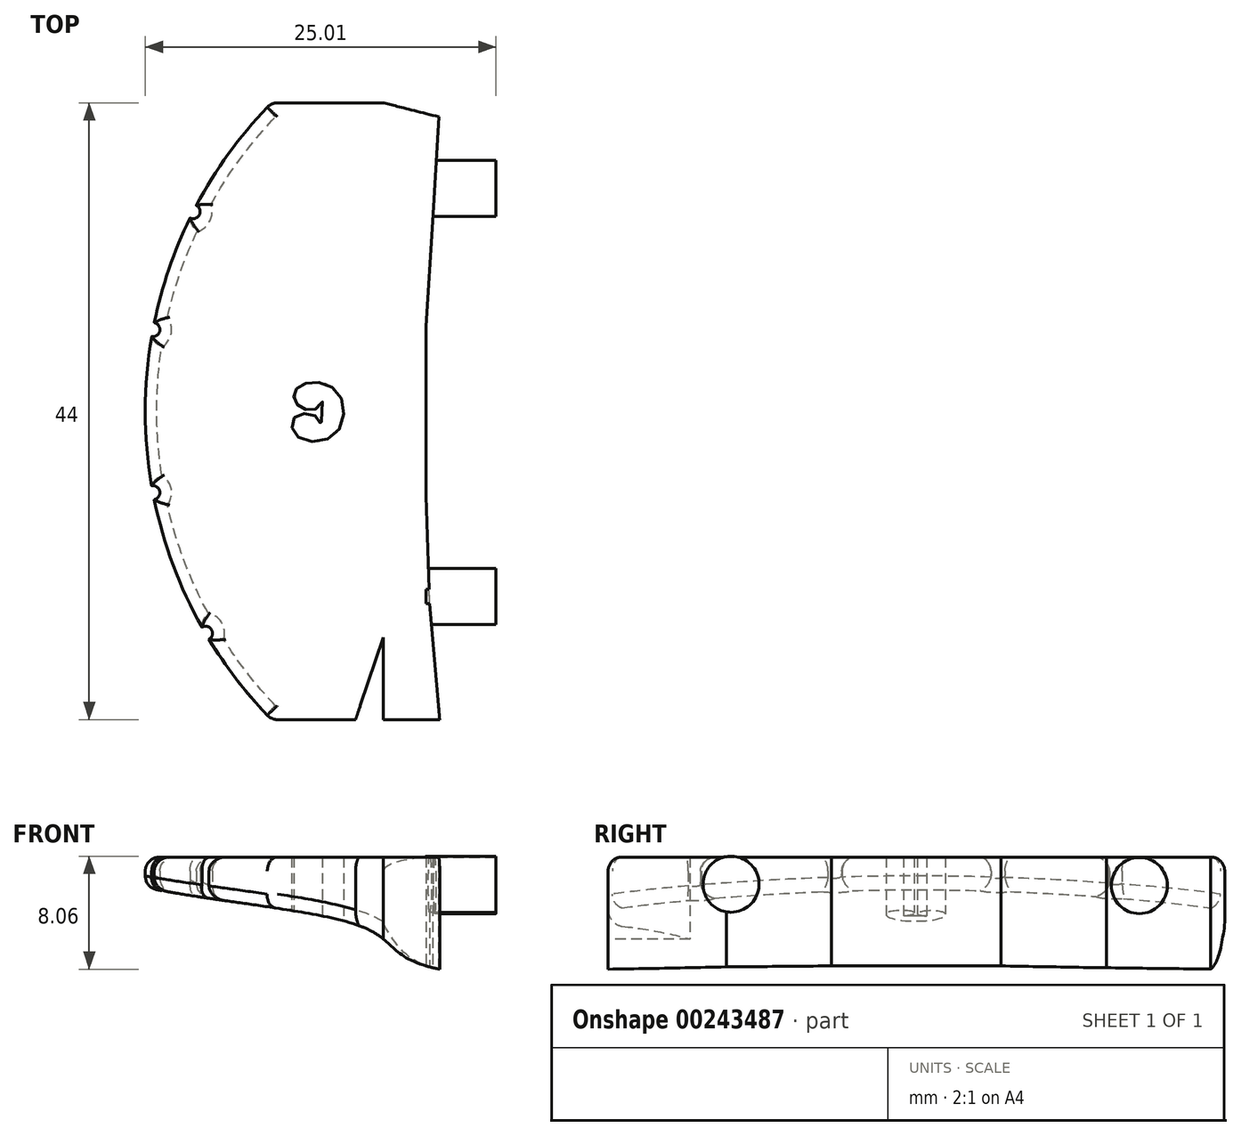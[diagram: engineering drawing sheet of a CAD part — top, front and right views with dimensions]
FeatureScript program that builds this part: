
annotation { "Feature Type Name" : "Feature", "Feature Type Description" : "" }
export const myFeature = defineFeature(function(context is Context, id is Id, definition is map)
    precondition{}
    {
        {
            var Q0;
            Q0=qCreatedBy(makeId("Top.planeOp"),FACE);
            var sketch = newSketch(context, id + "F0", { "sketchPlane" : qUnion([Q0])});
            skLineSegment(sketch, "E0.bottom", {"start": v(0, 0) * mm, "end": v(12, 0) * mm});
            skLineSegment(sketch, "E0.top", {"start": v(0, 44) * mm, "end": v(12, 44) * mm});
            skLineSegment(sketch, "E0.left", {"start": v(0, 0) * mm, "end": v(0, 44) * mm});
            skLineSegment(sketch, "E0.right", {"start": v(12, 0) * mm, "end": v(12, 44) * mm});
            skPoint(sketch, "E1", {"position": v(0, 22) * mm});
            skArc(sketch, "E2", {"start": v(0, 44) * mm, "mid": v(-9, 22) * mm, "end": v(0, 0) * mm});
            skLineSegment(sketch, "E3", {"start": v(0, 0) * mm, "end": v(0, 3.52) * mm, "construction": true});
            skLineSegment(sketch, "E4", {"start": v(0, 40.48) * mm, "end": v(0, 44) * mm, "construction": true});
            skLineSegment(sketch, "E5", {"start": v(18.87, 22) * mm, "end": v(22.39, 22) * mm, "construction": true});
            skPoint(sketch, "E6", {"position": v(-9, 22) * mm});
            skCircle(sketch, "E7", {"center": v(-5.59, 36.24) * mm, "radius": 0.5 * mm});
            skCircle(sketch, "E8", {"center": v(-8.45, 27.82) * mm, "radius": 0.5 * mm});
            skCircle(sketch, "E9", {"center": v(-8.46, 16.2) * mm, "radius": 0.5 * mm});
            skCircle(sketch, "E10", {"center": v(-4.71, 6.16) * mm, "radius": 0.5 * mm});
            skPoint(sketch, "E11", {"position": v(0, 40.69) * mm});
            skLineSegment(sketch, "E12", {"start": v(12, 44) * mm, "end": v(11.52, 35.55) * mm});
            skLineSegment(sketch, "E13", {"start": v(11.52, 35.55) * mm, "end": v(11.01, 28.04) * mm});
            skLineSegment(sketch, "E14", {"start": v(11.01, 28.04) * mm, "end": v(11.01, 15.95) * mm});
            skLineSegment(sketch, "E15", {"start": v(11.01, 15.95) * mm, "end": v(11.28, 8.43) * mm});
            skLineSegment(sketch, "E16", {"start": v(11.28, 8.43) * mm, "end": v(12, 0) * mm});
            skLineSegment(sketch, "E17", {"start": v(7.97, 0) * mm, "end": v(7.97, 5.86) * mm});
            skLineSegment(sketch, "E18", {"start": v(7.97, 5.86) * mm, "end": v(6, 0) * mm});
            skFitSpline(sketch, "E19", {"points": [v(3.6, 22) * mm, v(3.63, 22.75) * mm, v(3.3, 22.24) * mm, v(2.12, 22.24) * mm, v(1.6, 23.16) * mm, v(2.47, 24) * mm, v(4.75, 23.31) * mm, v(4.57, 20.39) * mm, v(1.82, 20.21) * mm, v(1.66, 21.56) * mm, v(3.15, 21.65) * mm, v(3.54, 21.08) * mm, v(3.6, 22) * mm]});
            skSolve(sketch);
        }
        {
            var Q0;
            Q0=makeQuery(id+"F0.imprint","IMPRINT",FACE,{"disambiguationData":[TD([[makeQuery(id+"F0.imprint","IMPRINT",EDGE,{"derivedFrom":sQuery(id+"F0.wireOp",EDGE,"E0.bottom")}),1.0]])]});
            var Q1;
            {var subQ8=sQuery(id+"F0.wireOp",EDGE,"E0.left");Q1=makeQuery(id+"F0.imprint","IMPRINT",FACE,{"disambiguationData":[TD([[makeQuery(id+"F0.imprint","IMPRINT",EDGE,{"derivedFrom":subQ8}),1.0]])]});}
            extrude(context, id + "F1", {"entities" : qUnion([Q0, Q1]), "depth" : 8 * mm, "offsetDistance" : 25 * mm});
        }
        {
            var Q0;
            Q0=makeQuery(id+"F1.opExtrude","SWEPT_FACE",FACE,{"disambiguationData":[OSD([sQuery(id+"F0.wireOp",EDGE,"E0.bottom")])]});
            var sketch = newSketch(context, id + "F2", { "sketchPlane" : qUnion([Q0])});
            skLineSegment(sketch, "E20.bottom", {"start": v(12, 0) * mm, "end": v(-10.64, 0) * mm});
            skLineSegment(sketch, "E20.left", {"start": v(12, 0) * mm, "end": v(12, 2.4) * mm});
            skLineSegment(sketch, "E21", {"start": v(12, 8) * mm, "end": v(12, 2.4) * mm});
            skLineSegment(sketch, "E22", {"start": v(-10.64, 6.2) * mm, "end": v(-10.64, 0) * mm});
            skPoint(sketch, "E23.1.internal.snap0", {"position": v(0, 4) * mm});
            skFitSpline(sketch, "E23", {"points": [v(-10.64, 6.2) * mm, v(7.08, 2.75) * mm, v(12, 0) * mm], "startDerivative": vector(27.55, -6.78) * mm, "endDerivative": vector(27.26, -5.3) * mm});
            skSolve(sketch);
        }
        {
            var Q0;
            Q0 = qSketchRegion(id + "F2", true);
            extrude(context, id + "F3", {"entities" : qUnion([Q0]), "operationType" : NewBodyOperationType.REMOVE, "oppositeDirection" : true, "depth" : 50 * mm, "offsetDistance" : 25 * mm});
        }
        {
            var Q0;
            Q0=makeQuery(id+"F1.opExtrude","CAP_EDGE",EDGE,{"disambiguationData":[OSD([sQuery(id+"F0.wireOp",EDGE,"E2")])],"isStart":false});
            var Q1;
            Q1=makeQuery(id+"F1.opExtrude","CAP_EDGE",EDGE,{"disambiguationData":[OSD([sQuery(id+"F0.wireOp",EDGE,"E7")])],"isStart":false});
            var Q2;
            Q2=makeQuery(id+"F3.boolean.opBoolean","INTERSECT",EDGE,{"derivedFrom":[makeQuery(id+"F1.opExtrude","SWEPT_FACE",FACE,{"disambiguationData":[OSD([sQuery(id+"F0.wireOp",EDGE,"E8")])]}),makeQuery(id+"F3.opExtrude","SWEPT_FACE",FACE,{"disambiguationData":[OSD([sQuery(id+"F2.wireOp",EDGE,"E23")])]})]});
            var Q3;
            Q3=makeQuery(id+"F1.opExtrude","CAP_EDGE",EDGE,{"disambiguationData":[OSD([sQuery(id+"F0.wireOp",EDGE,"E8")])],"isStart":false});
            var Q4;
            Q4=makeQuery(id+"F3.boolean.opBoolean","INTERSECT",EDGE,{"derivedFrom":[makeQuery(id+"F1.opExtrude","SWEPT_FACE",FACE,{"disambiguationData":[OSD([sQuery(id+"F0.wireOp",EDGE,"E9")])]}),makeQuery(id+"F3.opExtrude","SWEPT_FACE",FACE,{"disambiguationData":[OSD([sQuery(id+"F2.wireOp",EDGE,"E23")])]})]});
            var Q5;
            Q5=makeQuery(id+"F3.boolean.opBoolean","INTERSECT",EDGE,{"derivedFrom":[makeQuery(id+"F1.opExtrude","SWEPT_FACE",FACE,{"disambiguationData":[OSD([sQuery(id+"F0.wireOp",EDGE,"E10")])]}),makeQuery(id+"F3.opExtrude","SWEPT_FACE",FACE,{"disambiguationData":[OSD([sQuery(id+"F2.wireOp",EDGE,"E23")])]})]});
            var Q6;
            Q6=makeQuery(id+"F1.opExtrude","CAP_EDGE",EDGE,{"disambiguationData":[OSD([sQuery(id+"F0.wireOp",EDGE,"E9")])],"isStart":false});
            var Q7;
            Q7=makeQuery(id+"F1.opExtrude","CAP_EDGE",EDGE,{"disambiguationData":[OSD([sQuery(id+"F0.wireOp",EDGE,"E10")])],"isStart":false});
            var Q8;
            {var subQ0=sQuery(id+"F0.wireOp",EDGE,"E2");Q8=makeQuery(id+"F3.boolean.opBoolean","INTERSECT",EDGE,{"derivedFrom":[makeQuery(id+"F1.opExtrude","SWEPT_FACE",FACE,{"disambiguationData":[OSD([subQ0]),TDD([makeQuery(id+"F0.imprint","IMPRINT",EDGE,{"disambiguationData":[TD([[makeQuery(id+"F0.imprint","INTERSECT",VERTEX,{"disambiguationData":[OD(1.0)],"derivedFrom":[subQ0,sQuery(id+"F0.wireOp",EDGE,"E7")]}),-1.0]])],"derivedFrom":subQ0})])]}),makeQuery(id+"F3.opExtrude","SWEPT_FACE",FACE,{"disambiguationData":[OSD([sQuery(id+"F2.wireOp",EDGE,"E23")])]})]});}
            var Q9;
            {var subQ0=sQuery(id+"F0.wireOp",EDGE,"E2");Q9=makeQuery(id+"F3.boolean.opBoolean","INTERSECT",EDGE,{"derivedFrom":[makeQuery(id+"F1.opExtrude","SWEPT_FACE",FACE,{"disambiguationData":[OSD([subQ0]),TDD([makeQuery(id+"F0.imprint","IMPRINT",EDGE,{"disambiguationData":[TD([[makeQuery(id+"F0.imprint","INTERSECT",VERTEX,{"disambiguationData":[OD(1.0)],"derivedFrom":[subQ0,sQuery(id+"F0.wireOp",EDGE,"E8")]}),-1.0]])],"derivedFrom":subQ0})])]}),makeQuery(id+"F3.opExtrude","SWEPT_FACE",FACE,{"disambiguationData":[OSD([sQuery(id+"F2.wireOp",EDGE,"E23")])]})]});}
            var Q10;
            {var subQ0=sQuery(id+"F0.wireOp",EDGE,"E2");Q10=makeQuery(id+"F3.boolean.opBoolean","INTERSECT",EDGE,{"derivedFrom":[makeQuery(id+"F1.opExtrude","SWEPT_FACE",FACE,{"disambiguationData":[OSD([subQ0]),TDD([makeQuery(id+"F0.imprint","IMPRINT",EDGE,{"disambiguationData":[TD([[makeQuery(id+"F0.imprint","INTERSECT",VERTEX,{"disambiguationData":[OD(1.0)],"derivedFrom":[subQ0,sQuery(id+"F0.wireOp",EDGE,"E9")]}),-1.0]])],"derivedFrom":subQ0})])]}),makeQuery(id+"F3.opExtrude","SWEPT_FACE",FACE,{"disambiguationData":[OSD([sQuery(id+"F2.wireOp",EDGE,"E23")])]})]});}
            var Q11;
            {var subQ0=sQuery(id+"F0.wireOp",EDGE,"E2");Q11=makeQuery(id+"F3.boolean.opBoolean","INTERSECT",EDGE,{"derivedFrom":[makeQuery(id+"F1.opExtrude","SWEPT_FACE",FACE,{"disambiguationData":[OSD([subQ0]),TDD([makeQuery(id+"F0.imprint","IMPRINT",EDGE,{"disambiguationData":[TD([[makeQuery(id+"F0.imprint","INTERSECT",VERTEX,{"disambiguationData":[OD(1.0)],"derivedFrom":[subQ0,sQuery(id+"F0.wireOp",EDGE,"E10")]}),-1.0]])],"derivedFrom":subQ0})])]}),makeQuery(id+"F3.opExtrude","SWEPT_FACE",FACE,{"disambiguationData":[OSD([sQuery(id+"F2.wireOp",EDGE,"E23")])]})]});}
            var Q12;
            {var subQ0=sQuery(id+"F0.wireOp",EDGE,"E2");Q12=makeQuery(id+"F3.boolean.opBoolean","INTERSECT",EDGE,{"derivedFrom":[makeQuery(id+"F1.opExtrude","SWEPT_FACE",FACE,{"disambiguationData":[OSD([subQ0]),TDD([makeQuery(id+"F0.imprint","IMPRINT",EDGE,{"disambiguationData":[TD([[makeQuery(id+"F0.imprint","INTERSECT",VERTEX,{"disambiguationData":[OD(0.0)],"derivedFrom":[subQ0,sQuery(id+"F0.wireOp",EDGE,"E7")]}),1.0]])],"derivedFrom":subQ0})])]}),makeQuery(id+"F3.opExtrude","SWEPT_FACE",FACE,{"disambiguationData":[OSD([sQuery(id+"F2.wireOp",EDGE,"E23")])]})]});}
            var Q13;
            Q13=makeQuery(id+"F3.boolean.opBoolean","INTERSECT",EDGE,{"derivedFrom":[makeQuery(id+"F1.opExtrude","SWEPT_FACE",FACE,{"disambiguationData":[OSD([sQuery(id+"F0.wireOp",EDGE,"E7")])]}),makeQuery(id+"F3.opExtrude","SWEPT_FACE",FACE,{"disambiguationData":[OSD([sQuery(id+"F2.wireOp",EDGE,"E23")])]})]});
            fillet(context, id + "F4", {"entities" : qUnion([Q0, Q1, Q2, Q3, Q4, Q5, Q6, Q7, Q8, Q9, Q10, Q11, Q12, Q13]), "tangentPropagation" : true, "radius" : 1 * mm, "defaultsChanged" : true, "vertexSettings" : [], "allowEdgeOverflow" : false});
        }
        {
            var Q0;
            Q0=makeQuery(id+"F1.opExtrude","SWEPT_FACE",FACE,{"disambiguationData":[OSD([sQuery(id+"F0.wireOp",EDGE,"E14")])]});
            var sketch = newSketch(context, id + "F5", { "sketchPlane" : qUnion([Q0])});
            skCircle(sketch, "E24", {"center": v(37.91, 5.97) * mm, "radius": 2 * mm});
            skCircle(sketch, "E25", {"center": v(8.78, 6.06) * mm, "radius": 2 * mm});
            skSolve(sketch);
        }
        {
            var Q0;
            Q0 = qSketchRegion(id + "F5", true);
            extrude(context, id + "F6", {"entities" : qUnion([Q0]), "operationType" : NewBodyOperationType.ADD, "depth" : 5 * mm, "offsetDistance" : 25 * mm});
        }
        {
            var Q0;
            Q0=makeQuery(id+"F1.opExtrude","SWEPT_EDGE",EDGE,{"disambiguationData":[OSD([sQuery(id+"F0.wireOp",EDGE,"E0.top"),sQuery(id+"F0.wireOp",EDGE,"E0.right"),sQuery(id+"F0.wireOp",EDGE,"E12")])]});
            chamfer(context, id + "F7", {"entities" : qUnion([Q0]), "chamferType" : ChamferType.TWO_OFFSETS, "width1" : 4 * mm, "oppositeDirection" : false, "width2" : 1 * mm});
        }
        {
            var Q0;
            {var subQ0=sQuery(id+"F0.wireOp",EDGE,"E0.bottom");Q0=makeQuery(id+"F1.opExtrude","CAP_EDGE",EDGE,{"disambiguationData":[OSD([subQ0]),TDD([makeQuery(id+"F0.imprint","IMPRINT",EDGE,{"disambiguationData":[TD([[makeQuery(id+"F0.imprint","INTERSECT",VERTEX,{"derivedFrom":[subQ0,sQuery(id+"F0.wireOp",EDGE,"E18")]}),1.0]])],"derivedFrom":subQ0})])],"isStart":false});}
            var Q1;
            {var subQ0=sQuery(id+"F0.wireOp",EDGE,"E0.bottom");var subQ1=sQuery(id+"F2.wireOp",EDGE,"E23");Q1=makeQuery(id+"F3.boolean.opBoolean","COPY",EDGE,{"disambiguationData":[topologyDisambiguationEdgeConnected([makeQuery(id+"F1.opExtrude","SWEPT_FACE",FACE,{"disambiguationData":[OSD([subQ0]),TDD([makeQuery(id+"F0.imprint","IMPRINT",EDGE,{"disambiguationData":[TD([[makeQuery(id+"F0.imprint","INTERSECT",VERTEX,{"derivedFrom":[subQ0,sQuery(id+"F0.wireOp",EDGE,"E18")]}),1.0]])],"derivedFrom":subQ0})])]})])],"derivedFrom":makeQuery(id+"F3.opExtrude","CAP_EDGE",EDGE,{"disambiguationData":[OSD([subQ1])],"isStart":true})});}
            var Q2;
            Q2=makeQuery(id+"FE60vN1aF7f0GQH_1.opChamfer","BLEND_EDGE",EDGE,{"blendedFrom":[makeQuery(id+"F1.opExtrude","SWEPT_EDGE",EDGE,{"disambiguationData":[OSD([sQuery(id+"F0.wireOp",EDGE,"E0.bottom"),sQuery(id+"F0.wireOp",EDGE,"E0.right"),sQuery(id+"F0.wireOp",EDGE,"E16")])]}),makeQuery(id+"F3.boolean.opBoolean","COPY",FACE,{"derivedFrom":makeQuery(id+"F3.opExtrude","SWEPT_FACE",FACE,{"disambiguationData":[OSD([sQuery(id+"F2.wireOp",EDGE,"E23")])]})})],"blendedInto":[makeQuery(id+"F3.boolean.opBoolean","COPY",FACE,{"derivedFrom":makeQuery(id+"F3.opExtrude","SWEPT_FACE",FACE,{"disambiguationData":[OSD([sQuery(id+"F2.wireOp",EDGE,"E23")])]})})]});
            var Q3;
            {var subQ0=sQuery(id+"F0.wireOp",EDGE,"E16");var subQ1=sQuery(id+"F0.wireOp",EDGE,"E0.bottom");Q3=makeQuery(id+"FE60vN1aF7f0GQH_1.opChamfer","BLEND_EDGE",EDGE,{"blendedFrom":[makeQuery(id+"F1.opExtrude","SWEPT_EDGE",EDGE,{"disambiguationData":[OSD([subQ1,sQuery(id+"F0.wireOp",EDGE,"E0.right"),subQ0])]}),makeQuery(id+"F1.opExtrude","CAP_FACE",FACE,{"disambiguationData":[OSD([subQ1,sQuery(id+"F0.wireOp",EDGE,"E0.top"),sQuery(id+"F0.wireOp",EDGE,"E2"),sQuery(id+"F0.wireOp",EDGE,"E7"),sQuery(id+"F0.wireOp",EDGE,"E8"),sQuery(id+"F0.wireOp",EDGE,"E9"),sQuery(id+"F0.wireOp",EDGE,"E10"),sQuery(id+"F0.wireOp",EDGE,"E12"),sQuery(id+"F0.wireOp",EDGE,"E13"),sQuery(id+"F0.wireOp",EDGE,"E14"),sQuery(id+"F0.wireOp",EDGE,"E15"),subQ0,sQuery(id+"F0.wireOp",EDGE,"E17"),sQuery(id+"F0.wireOp",EDGE,"E18")])],"isStart":false})],"blendedInto":[makeQuery(id+"F1.opExtrude","CAP_FACE",FACE,{"disambiguationData":[OSD([subQ1,sQuery(id+"F0.wireOp",EDGE,"E0.top"),sQuery(id+"F0.wireOp",EDGE,"E2"),sQuery(id+"F0.wireOp",EDGE,"E7"),sQuery(id+"F0.wireOp",EDGE,"E8"),sQuery(id+"F0.wireOp",EDGE,"E9"),sQuery(id+"F0.wireOp",EDGE,"E10"),sQuery(id+"F0.wireOp",EDGE,"E12"),sQuery(id+"F0.wireOp",EDGE,"E13"),sQuery(id+"F0.wireOp",EDGE,"E14"),sQuery(id+"F0.wireOp",EDGE,"E15"),subQ0,sQuery(id+"F0.wireOp",EDGE,"E17"),sQuery(id+"F0.wireOp",EDGE,"E18")])],"isStart":false})]});}
            var Q4;
            Q4=makeQuery(id+"F1.opExtrude","CAP_EDGE",EDGE,{"disambiguationData":[OSD([sQuery(id+"F0.wireOp",EDGE,"E0.top")])],"isStart":false});
            var Q5;
            Q5=makeQuery(id+"F3.boolean.opBoolean","INTERSECT",EDGE,{"derivedFrom":[makeQuery(id+"F1.opExtrude","SWEPT_FACE",FACE,{"disambiguationData":[OSD([sQuery(id+"F0.wireOp",EDGE,"E0.top")])]}),makeQuery(id+"F3.opExtrude","SWEPT_FACE",FACE,{"disambiguationData":[OSD([sQuery(id+"F2.wireOp",EDGE,"E23")])]})]});
            var Q6;
            {var subQ0=sQuery(id+"F0.wireOp",EDGE,"E0.bottom");var subQ1=sQuery(id+"F2.wireOp",EDGE,"E23");Q6=makeQuery(id+"F3.boolean.opBoolean","COPY",EDGE,{"disambiguationData":[topologyDisambiguationEdgeConnected([makeQuery(id+"F1.opExtrude","SWEPT_FACE",FACE,{"disambiguationData":[OSD([subQ0]),TDD([makeQuery(id+"F0.imprint","IMPRINT",EDGE,{"disambiguationData":[TD([[makeQuery(id+"F0.imprint","INTERSECT",VERTEX,{"derivedFrom":[subQ0,sQuery(id+"F0.wireOp",EDGE,"E17")]}),-1.0]])],"derivedFrom":subQ0})])]})])],"derivedFrom":makeQuery(id+"F3.opExtrude","CAP_EDGE",EDGE,{"disambiguationData":[OSD([subQ1])],"isStart":true})});}
            var Q7;
            {var subQ0=sQuery(id+"F0.wireOp",EDGE,"E0.bottom");Q7=makeQuery(id+"F1.opExtrude","CAP_EDGE",EDGE,{"disambiguationData":[OSD([subQ0]),TDD([makeQuery(id+"F0.imprint","IMPRINT",EDGE,{"disambiguationData":[TD([[makeQuery(id+"F0.imprint","INTERSECT",VERTEX,{"derivedFrom":[subQ0,sQuery(id+"F0.wireOp",EDGE,"E17")]}),-1.0]])],"derivedFrom":subQ0})])],"isStart":false});}
            fillet(context, id + "F8", {"entities" : qUnion([Q0, Q1, Q2, Q3, Q4, Q5, Q6, Q7]), "tangentPropagation" : true, "radius" : 1 * mm, "defaultsChanged" : false, "vertexSettings" : [], "allowEdgeOverflow" : false});
        }
    });
